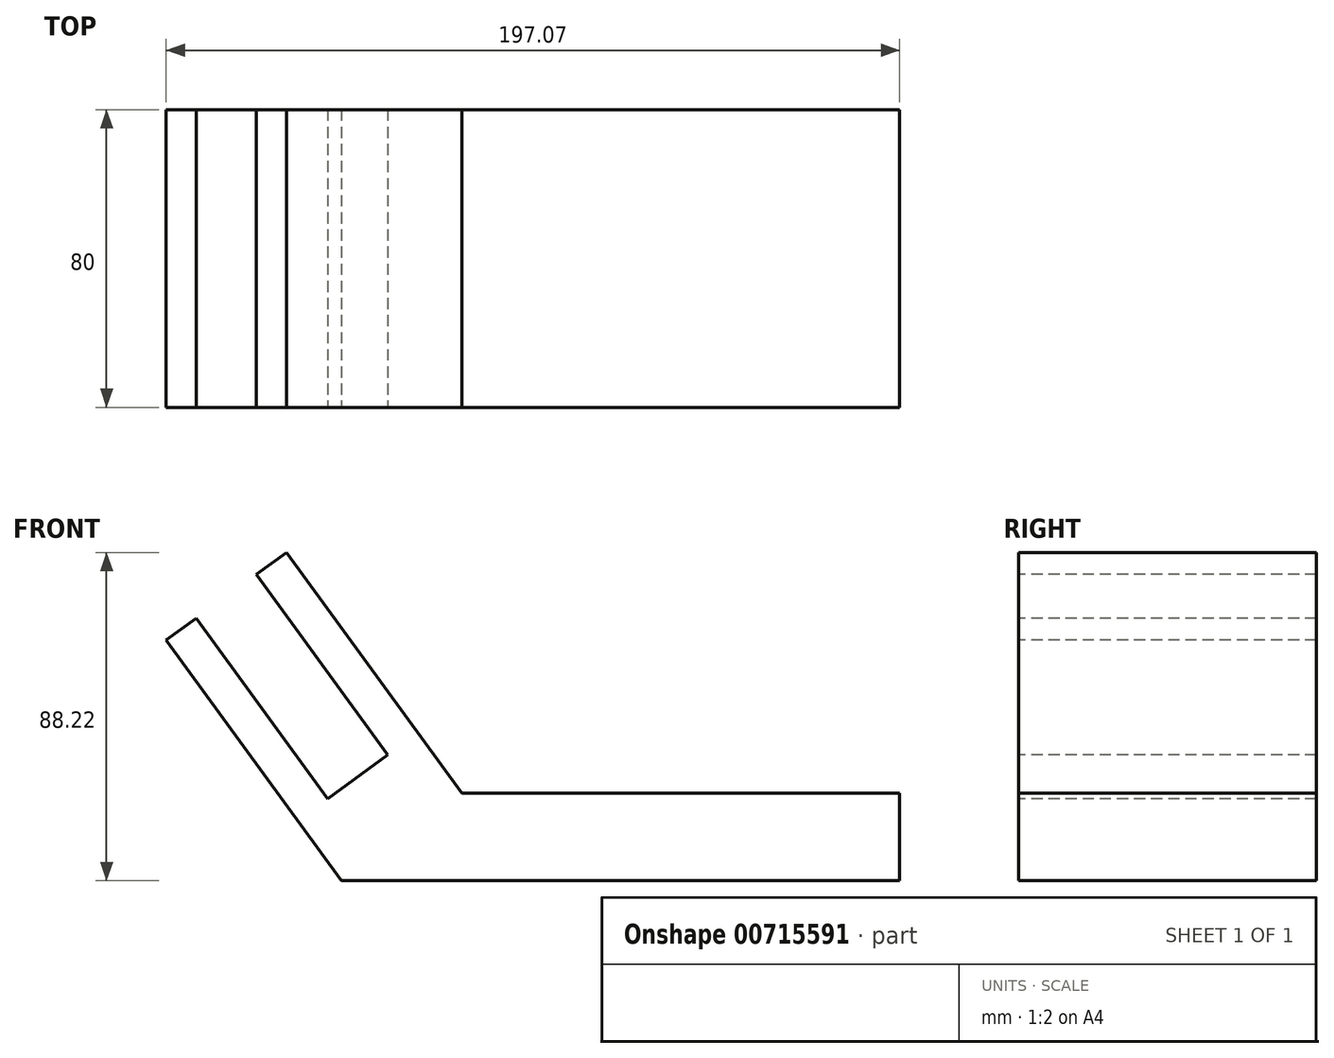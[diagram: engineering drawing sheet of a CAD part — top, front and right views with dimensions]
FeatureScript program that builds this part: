
annotation { "Feature Type Name" : "Feature", "Feature Type Description" : "" }
export const myFeature = defineFeature(function(context is Context, id is Id, definition is map)
    precondition{}
    {
        {
            var Q0;
            Q0=qCreatedBy(makeId("Front.planeOp"),FACE);
            var sketch = newSketch(context, id + "F0", { "sketchPlane" : qUnion([Q0])});
            skLineSegment(sketch, "E0", {"start": v(-75.21, -33.97) * mm, "end": v(74.79, -33.97) * mm});
            skLineSegment(sketch, "E1", {"start": v(74.79, -33.97) * mm, "end": v(74.79, -23.97) * mm});
            skLineSegment(sketch, "E2", {"start": v(-75.21, -33.97) * mm, "end": v(-122.28, 30.71) * mm});
            skLineSegment(sketch, "E3", {"start": v(-122.28, 30.71) * mm, "end": v(-114.2, 36.6) * mm});
            skLineSegment(sketch, "E4", {"start": v(-114.2, 36.6) * mm, "end": v(-78.9, -11.91) * mm});
            skLineSegment(sketch, "E5", {"start": v(-78.9, -11.91) * mm, "end": v(-62.72, -0.15) * mm});
            skLineSegment(sketch, "E6", {"start": v(-62.72, -0.15) * mm, "end": v(-98.03, 48.37) * mm});
            skLineSegment(sketch, "E7", {"start": v(-98.03, 48.37) * mm, "end": v(-89.94, 54.25) * mm});
            skLineSegment(sketch, "E8", {"start": v(-89.94, 54.25) * mm, "end": v(-42.87, -10.43) * mm});
            skLineSegment(sketch, "E9", {"start": v(-42.87, -10.43) * mm, "end": v(74.79, -10.43) * mm});
            skLineSegment(sketch, "E10", {"start": v(74.79, -10.43) * mm, "end": v(74.79, -23.97) * mm});
            skSolve(sketch);
        }
        {
            var Q0;
            Q0 = qSketchRegion(id + "F0", true);
            extrude(context, id + "F1", {"entities" : qUnion([Q0]), "oppositeDirection" : true, "depth" : 80 * mm, "offsetDistance" : 25 * mm});
        }
    });
